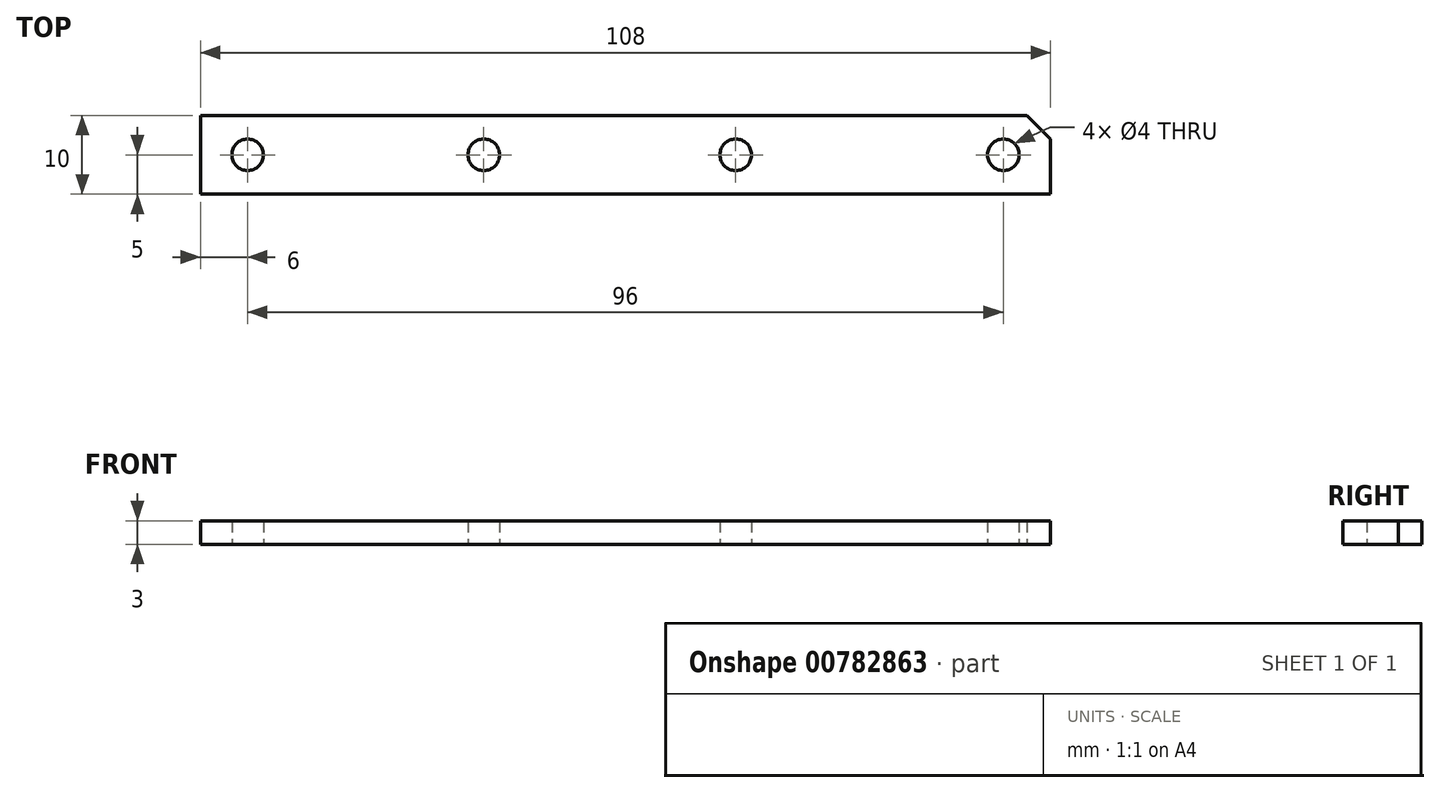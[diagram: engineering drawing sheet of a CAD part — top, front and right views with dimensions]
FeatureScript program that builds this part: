
annotation { "Feature Type Name" : "Feature", "Feature Type Description" : "" }
export const myFeature = defineFeature(function(context is Context, id is Id, definition is map)
    precondition{}
    {
        {
            var Q0;
            Q0=qCreatedBy(makeId("Top.planeOp"),FACE);
            var sketch = newSketch(context, id + "F0", { "sketchPlane" : qUnion([Q0])});
            skLineSegment(sketch, "E0.bottom", {"start": v(-54, 5) * mm, "end": v(54, 5) * mm});
            skLineSegment(sketch, "E0.top", {"start": v(-54, -5) * mm, "end": v(54, -5) * mm});
            skLineSegment(sketch, "E0.left", {"start": v(-54, 5) * mm, "end": v(-54, -5) * mm});
            skLineSegment(sketch, "E0.right", {"start": v(54, 5) * mm, "end": v(54, -5) * mm});
            skPoint(sketch, "E0.middle", {"position": v(0, 0) * mm});
            skCircle(sketch, "E1", {"center": v(-18, 0) * mm, "radius": 2 * mm});
            skCircle(sketch, "E2", {"center": v(48, 0) * mm, "radius": 2 * mm});
            skCircle(sketch, "E3", {"center": v(14, 0) * mm, "radius": 2 * mm});
            skCircle(sketch, "E4", {"center": v(-48, 0) * mm, "radius": 2 * mm});
            skSolve(sketch);
        }
        {
            var Q0;
            Q0=makeQuery(id+"F0.imprint","IMPRINT",FACE,{"disambiguationData":[TD([[makeQuery(id+"F0.imprint","IMPRINT",EDGE,{"derivedFrom":sQuery(id+"F0.wireOp",EDGE,"E0.bottom")}),-1.0]])]});
            extrude(context, id + "F1", {"entities" : qUnion([Q0]), "depth" : 3 * mm, "offsetDistance" : 25 * mm});
        }
        {
            var Q0;
            Q0=makeQuery(id+"F1.opExtrude","SWEPT_EDGE",EDGE,{"disambiguationData":[OSD([sQuery(id+"F0.wireOp",EDGE,"E0.bottom"),sQuery(id+"F0.wireOp",EDGE,"E0.right")])]});
            chamfer(context, id + "F2", {"entities" : qUnion([Q0]), "width" : 3 * mm, "tangentPropagation" : true});
        }
    });
